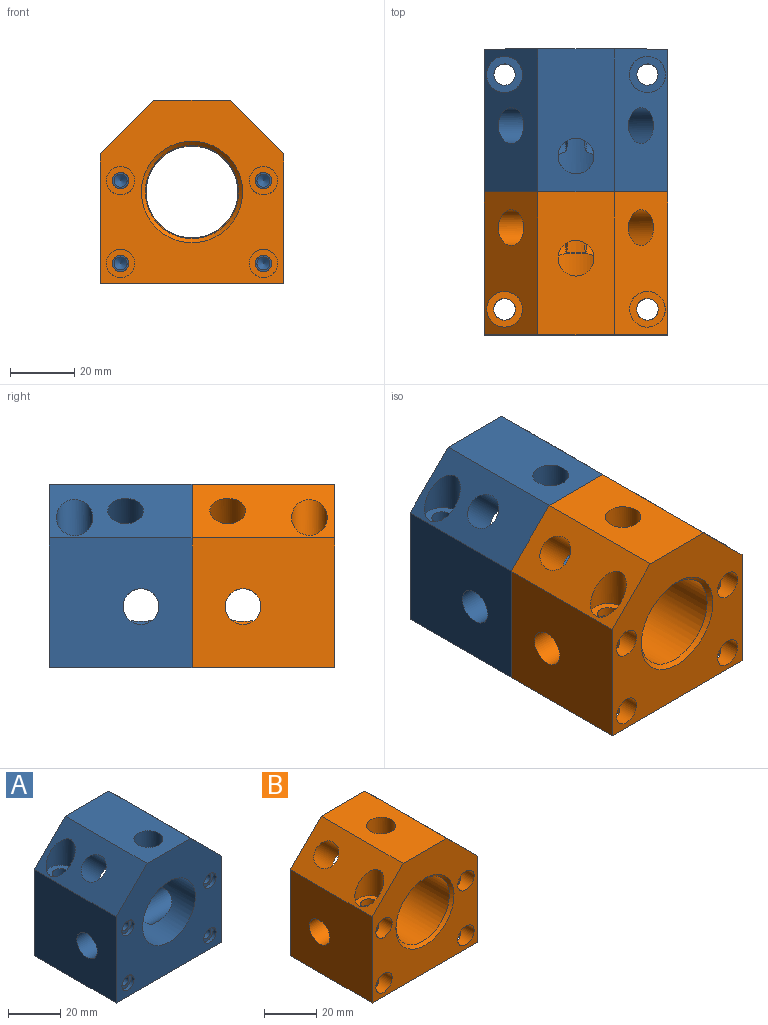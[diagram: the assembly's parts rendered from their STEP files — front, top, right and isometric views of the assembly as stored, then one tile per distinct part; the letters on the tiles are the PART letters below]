
ASSEMBLY  parts=2 mates=1
PART A: 44 faces, bbox 57.2x44.5x57.2 mm
  f0: cylinder r=14.29mm len=28.58mm, axis (0,-1,0), area 1303mm2, adj f1,f2,f3,f4,f12,f15,f16,f17
  f1: cone r=0mm half-angle=59deg, axis (0,1,0), area 2.8mm2, adj f0,f5,f19,f20
  f2: cone r=0mm half-angle=59deg, axis (0,1,0), area 2.6mm2, adj f0,f5,f18,f20
  f3: cone r=0mm half-angle=59deg, axis (0,1,0), area 2.6mm2, adj f0,f5,f15,f19
  f4: cone r=0mm half-angle=59deg, axis (0,1,0), area 1.5mm2, adj f0,f5,f15,f16,f17,f18
  f5: cylinder r=14.49mm len=28.98mm, axis (0,1,0), area 2018mm2, adj f1,f2,f3,f4,f14,f15,f18,f19
  f6: plane 44.45x40.41mm, normal (-1,0,0), area 1699.1mm2, adj f7,f11,f12,f13,f15
  f7: plane 57.15x44.45mm, normal (0,0,-1), area 2471.9mm2, adj f6,f8,f12,f13,f22,f26
  f8: plane 44.45x40.41mm, normal (1,0,0), area 1699.1mm2, adj f7,f9,f12,f13,f18
  f9: plane 44.45x16.74mm, normal (0.71,0,0.71), area 814.4mm2, adj f8,f10,f12,f13,f20,f25
  f10: plane 44.45x23.67mm, normal (0,0,1), area 955mm2, adj f9,f11,f12,f13,f21
  f11: plane 44.45x16.74mm, normal (-0.71,0,0.71), area 814.4mm2, adj f6,f10,f12,f13,f19,f24
  f12: plane 57.15x57.15mm, normal (0,-1,0), area 2206.6mm2, adj f0,f6,f7,f8,f9,f10,f11,f30
  f13: plane 57.15x57.15mm, normal (0,1,0), area 2205.6mm2, adj f6,f7,f8,f9,f10,f11,f14
  f14: cone r=14.49mm half-angle=45deg, axis (0,1,0), area 170.7mm2, adj f5,f13
  f15: cylinder r=5.56mm len=25.4mm, axis (-1,0,0), area 671.5mm2, adj f0,f3,f4,f5,f6,f16
  f16: cone r=0mm half-angle=59deg, axis (-1,0,0), area 5.6mm2, adj f0,f4,f15
  f17: cone r=0mm half-angle=59deg, axis (1,0,0), area 5.6mm2, adj f0,f4,f18
  f18: cylinder r=5.56mm len=25.4mm, axis (1,0,0), area 671.3mm2, adj f0,f2,f4,f5,f8,f17
  f19: cylinder r=5.56mm len=18.69mm, axis (-0.71,0,0.71), area 514.4mm2, adj f0,f1,f3,f5,f11
  f20: cylinder r=5.56mm len=18.69mm, axis (0.71,0,0.71), area 514.4mm2, adj f0,f1,f2,f5,f9
  f21: cylinder r=5.56mm len=15.42mm, axis (0,0,1), area 538.8mm2, adj f0,f10
  f22: cylinder r=3.3mm len=39.37mm, axis (0,0,1), area 816.3mm2, adj f7,f23
  f23: plane 11.25x11.25mm, normal (0,0,1), area 65.2mm2, adj f22,f24
  f24: cylinder r=5.62mm len=13.02mm, axis (0,0,1), area 261.2mm2, adj f11,f23
  f25: cylinder r=5.62mm len=13.02mm, axis (0,0,1), area 261.2mm2, adj f9,f27
  f26: cylinder r=3.3mm len=39.37mm, axis (0,0,1), area 816.3mm2, adj f7,f27
  f27: plane 11.25x11.25mm, normal (0,0,1), area 65.2mm2, adj f25,f26
  f28: cylinder r=2.02mm len=22.54mm, axis (0,-1,0), area 286mm2, adj f29,f31
  f29: plane 6.63x6.63mm, normal (0,-1,0), area 21.7mm2, adj f28,f30
  f30: cylinder r=3.31mm len=6.63mm, axis (0,-1,0), area 33.1mm2, adj f12,f29
  f31: cone r=0mm half-angle=59deg, axis (0,-1,0), area 14.9mm2, adj f28
  f32: cylinder r=2.02mm len=22.54mm, axis (0,-1,0), area 286mm2, adj f33,f35
  f33: plane 6.63x6.63mm, normal (0,-1,0), area 21.7mm2, adj f32,f34
  f34: cylinder r=3.31mm len=6.63mm, axis (0,-1,0), area 33.1mm2, adj f12,f33
  f35: cone r=0mm half-angle=59deg, axis (0,-1,0), area 14.9mm2, adj f32
  f36: cylinder r=2.02mm len=22.54mm, axis (0,-1,0), area 286mm2, adj f37,f39
  f37: plane 6.63x6.63mm, normal (0,-1,0), area 21.7mm2, adj f36,f38
  f38: cylinder r=3.31mm len=6.63mm, axis (0,-1,0), area 33.1mm2, adj f12,f37
  f39: cone r=0mm half-angle=59deg, axis (0,-1,0), area 14.9mm2, adj f36
  f40: cylinder r=2.02mm len=22.54mm, axis (0,-1,0), area 286mm2, adj f41,f43
  f41: plane 6.63x6.63mm, normal (0,-1,0), area 21.7mm2, adj f40,f42
  f42: cylinder r=3.31mm len=6.63mm, axis (0,-1,0), area 33.1mm2, adj f12,f41
  f43: cone r=0mm half-angle=59deg, axis (0,-1,0), area 14.9mm2, adj f40
PART B: 55 faces, bbox 57.2x44.5x57.2 mm
  f0: plane 31.75x31.75mm, normal (0,1,0), area 150.4mm2, adj f9,f52
  f1: cylinder r=2.55mm len=5.11mm, axis (0,-1,0), area 14.3mm2, adj f34,f50
  f2: cylinder r=2.55mm len=5.11mm, axis (0,-1,0), area 14.3mm2, adj f37,f48
  f3: cylinder r=2.55mm len=5.11mm, axis (0,-1,0), area 14.3mm2, adj f39,f46
  f4: cylinder r=2.55mm len=5.11mm, axis (0,-1,0), area 14.3mm2, adj f42,f44
  f5: cylinder r=3.38mm len=6.76mm, axis (0,0,1), area 57.2mm2, adj f15,f43
  f6: cylinder r=3.38mm len=6.76mm, axis (0,0,1), area 75.6mm2, adj f24,f40
  f7: cylinder r=3.38mm len=6.76mm, axis (0,0,1), area 57.2mm2, adj f15,f38
  f8: cylinder r=3.38mm len=6.76mm, axis (0,0,1), area 75.6mm2, adj f25,f35
  f9: cylinder r=14.29mm len=28.58mm, axis (0,1,0), area 1244.2mm2, adj f0,f10,f11,f12,f27,f28,f29,f30
  f10: cone r=0mm half-angle=59deg, axis (0,-1,0), area 5.3mm2, adj f9,f13,f27,f31
  f11: cone r=0mm half-angle=59deg, axis (0,-1,0), area 5.3mm2, adj f9,f13,f30,f31
  f12: cone r=0mm half-angle=59deg, axis (0,-1,0), area 1.5mm2, adj f9,f13,f27,f28,f29,f30
  f13: cylinder r=14.49mm len=28.98mm, axis (0,-1,0), area 2085.2mm2, adj f10,f11,f12,f22,f27,f30,f31
  f14: plane 44.45x40.41mm, normal (-1,0,0), area 1699.1mm2, adj f15,f19,f20,f21,f27
  f15: plane 57.15x44.45mm, normal (0,0,-1), area 2468.6mm2, adj f5,f7,f14,f16,f20,f21
  f16: plane 44.45x40.41mm, normal (1,0,0), area 1699.1mm2, adj f15,f17,f20,f21,f30
  f17: plane 44.45x16.74mm, normal (0.71,0,0.71), area 817.8mm2, adj f16,f18,f20,f21,f26,f33
  f18: plane 44.45x23.67mm, normal (0,0,1), area 955mm2, adj f17,f19,f20,f21,f31
  f19: plane 44.45x16.74mm, normal (-0.71,0,0.71), area 817.8mm2, adj f14,f18,f20,f21,f23,f32
  f20: plane 57.15x57.15mm, normal (0,1,0), area 1722.9mm2, adj f14,f15,f16,f17,f18,f19,f45,f47
  f21: plane 57.15x57.15mm, normal (0,-1,0), area 1960.1mm2, adj f14,f15,f16,f17,f18,f19,f22,f35
  f22: cone r=14.49mm half-angle=45deg, axis (0,-1,0), area 170.7mm2, adj f13,f21
  f23: cylinder r=5.56mm len=12.95mm, axis (0,0,1), area 258mm2, adj f19,f24
  f24: plane 11.11x11.11mm, normal (0,0,1), area 61.1mm2, adj f6,f23
  f25: plane 11.11x11.11mm, normal (0,0,1), area 61.1mm2, adj f8,f26
  f26: cylinder r=5.56mm len=12.95mm, axis (0,0,1), area 258mm2, adj f17,f25
  f27: cylinder r=5.56mm len=25.4mm, axis (-1,0,0), area 671.5mm2, adj f9,f10,f12,f13,f14,f28
  f28: cone r=0mm half-angle=59deg, axis (-1,0,0), area 5.6mm2, adj f9,f12,f27
  f29: cone r=0mm half-angle=59deg, axis (1,0,0), area 5.6mm2, adj f9,f12,f30
  f30: cylinder r=5.56mm len=25.4mm, axis (1,0,0), area 671.3mm2, adj f9,f11,f12,f13,f16,f29
  f31: cylinder r=5.56mm len=15.3mm, axis (0,0,1), area 514.4mm2, adj f9,f10,f11,f13,f18
  f32: cylinder r=5.56mm len=18.77mm, axis (-0.71,0,0.71), area 538.8mm2, adj f9,f19
  f33: cylinder r=5.56mm len=18.77mm, axis (0.71,0,0.71), area 538.8mm2, adj f9,f17
  f34: plane 8.84x8.84mm, normal (0,-1,0), area 40.9mm2, adj f1,f35
  f35: cylinder r=4.42mm len=22.23mm, axis (0,-1,0), area 545.2mm2, adj f8,f21,f34,f36
  f36: cylinder r=3.38mm len=20.08mm, axis (0,0,1), area 391.6mm2, adj f35,f38
  f37: plane 8.84x8.84mm, normal (0,-1,0), area 40.9mm2, adj f2,f38
  f38: cylinder r=4.42mm len=22.23mm, axis (0,-1,0), area 545.2mm2, adj f7,f21,f36,f37
  f39: plane 8.84x8.84mm, normal (0,-1,0), area 40.9mm2, adj f3,f40
  f40: cylinder r=4.42mm len=22.23mm, axis (0,-1,0), area 545.2mm2, adj f6,f21,f39,f41
  f41: cylinder r=3.38mm len=20.08mm, axis (0,0,1), area 391.6mm2, adj f40,f43
  f42: plane 8.84x8.84mm, normal (0,-1,0), area 40.9mm2, adj f4,f43
  f43: cylinder r=4.42mm len=22.23mm, axis (0,-1,0), area 545.2mm2, adj f5,f21,f41,f42
  f44: plane 6.63x6.63mm, normal (0,1,0), area 14mm2, adj f4,f45
  f45: cylinder r=3.31mm len=21.34mm, axis (0,1,0), area 444.4mm2, adj f20,f44
  f46: plane 6.63x6.63mm, normal (0,1,0), area 14mm2, adj f3,f47
  f47: cylinder r=3.31mm len=21.34mm, axis (0,1,0), area 444.4mm2, adj f20,f46
  f48: plane 6.63x6.63mm, normal (0,1,0), area 14mm2, adj f2,f49
  f49: cylinder r=3.31mm len=21.34mm, axis (0,1,0), area 444.4mm2, adj f20,f48
  f50: plane 6.63x6.63mm, normal (0,1,0), area 14mm2, adj f1,f51
  f51: cylinder r=3.31mm len=21.34mm, axis (0,1,0), area 444.4mm2, adj f20,f50
  f52: cylinder r=15.88mm len=31.75mm, axis (0,1,0), area 202.7mm2, adj f0,f54
  f53: cylinder r=18.92mm len=37.85mm, axis (0,1,0), area 241.6mm2, adj f20,f54
  f54: plane 37.85x37.85mm, normal (0,1,0), area 333.2mm2, adj f52,f53
PLACE A at identity fixed
PLACE B t=(0,-88.9,0)mm
MATE fastened B.f9 <-> A.f0  axis (0,1,0) through (0,-44.45,0)mm
